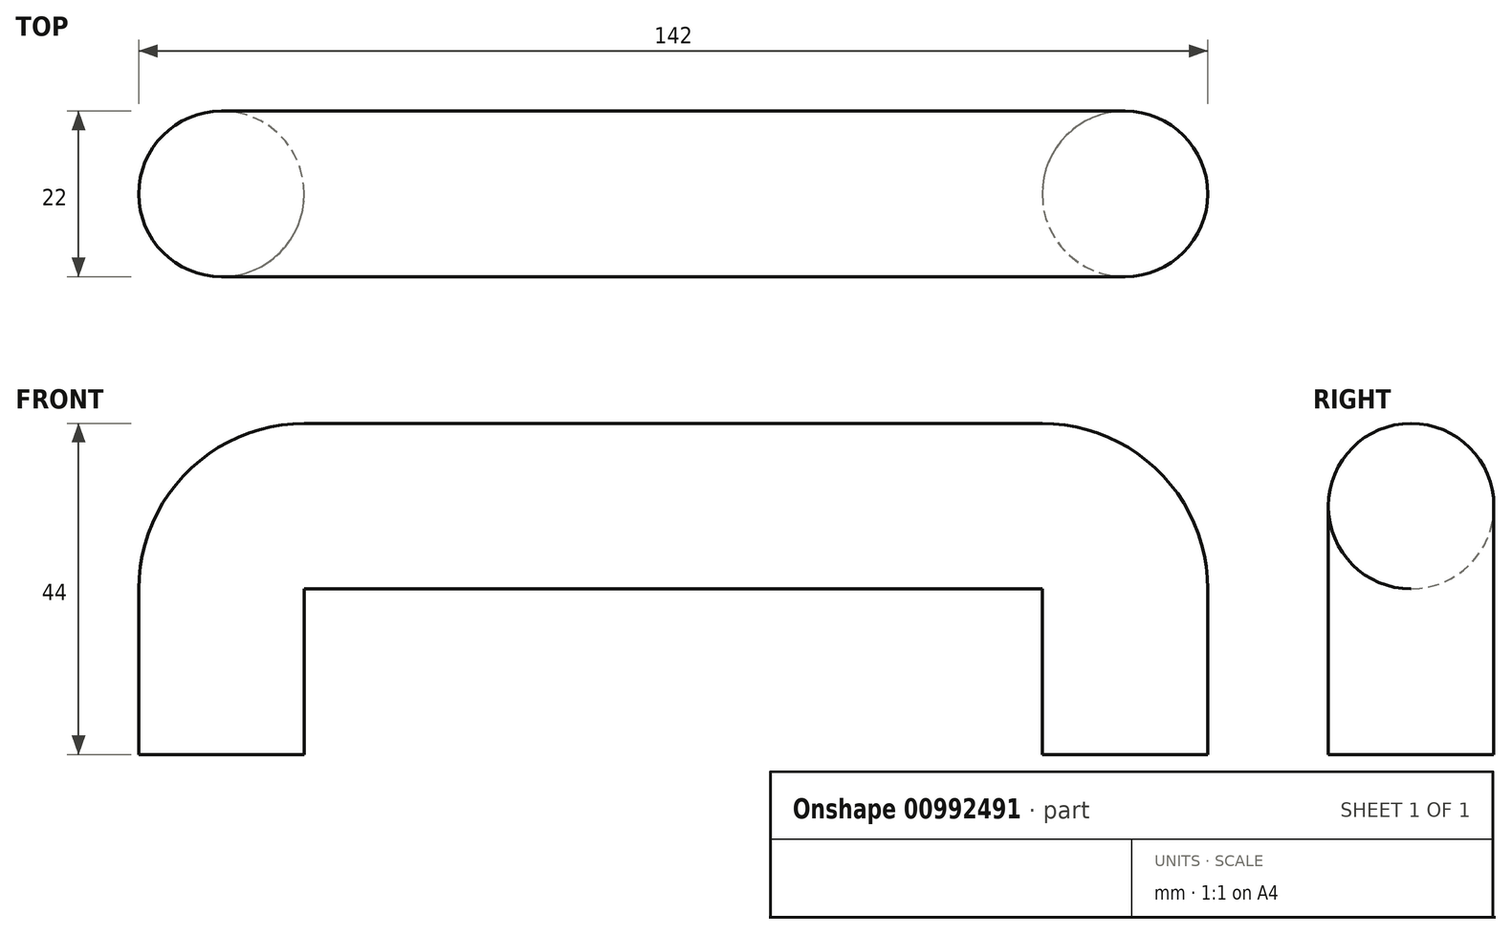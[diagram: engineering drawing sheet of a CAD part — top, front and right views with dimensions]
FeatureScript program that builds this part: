
annotation { "Feature Type Name" : "Feature", "Feature Type Description" : "" }
export const myFeature = defineFeature(function(context is Context, id is Id, definition is map)
    precondition{}
    {
        {
            var Q0;
            Q0=qCreatedBy(makeId("Top.planeOp"),FACE);
            var sketch = newSketch(context, id + "F0", { "sketchPlane" : qUnion([Q0])});
            skCircle(sketch, "E0", {"center": v(0, 0) * mm, "radius": 11 * mm});
            skSolve(sketch);
        }
        {
            var Q0;
            Q0=qCreatedBy(makeId("Front.planeOp"),FACE);
            var sketch = newSketch(context, id + "F1", { "sketchPlane" : qUnion([Q0])});
            skLineSegment(sketch, "E1", {"start": v(0, 0) * mm, "end": v(0, 22) * mm});
            skLineSegment(sketch, "E2", {"start": v(-11, 33) * mm, "end": v(-109, 33) * mm});
            skLineSegment(sketch, "E3", {"start": v(-120, 33) * mm, "end": v(-120, 33) * mm});
            skLineSegment(sketch, "E4", {"start": v(-120, 22) * mm, "end": v(-120, 0) * mm});
            skPoint(sketch, "E5.visualSharp", {"position": v(-120, 33) * mm});
            skArc(sketch, "E5.filletArc", {"start": v(-109, 33) * mm, "mid": v(-116.78, 29.78) * mm, "end": v(-120, 22) * mm});
            skPoint(sketch, "E6.visualSharp", {"position": v(0, 33) * mm});
            skArc(sketch, "E6.filletArc", {"start": v(0, 22) * mm, "mid": v(-3.22, 29.78) * mm, "end": v(-11, 33) * mm});
            skSolve(sketch);
        }
        {
            var Q0;
            Q0=makeQuery(id+"F0.imprint","IMPRINT",FACE,{"disambiguationData":[TD([[makeQuery(id+"F0.imprint","IMPRINT",EDGE,{"derivedFrom":sQuery(id+"F0.wireOp",EDGE,"E0")}),1.0]])]});
            var Q1;
            Q1=sQuery(id+"F1.wireOp",EDGE,"E1");
            var Q2;
            Q2=sQuery(id+"F1.wireOp",EDGE,"E6.filletArc");
            var Q3;
            Q3=sQuery(id+"F1.wireOp",EDGE,"E2");
            var Q4;
            Q4=sQuery(id+"F1.wireOp",EDGE,"E5.filletArc");
            var Q5;
            Q5=sQuery(id+"F1.wireOp",EDGE,"E4");
            sweep(context, id + "F2", {"profiles" : qUnion([Q0]), "path" : qUnion([Q1, Q2, Q3, Q4, Q5])});
        }
    });
